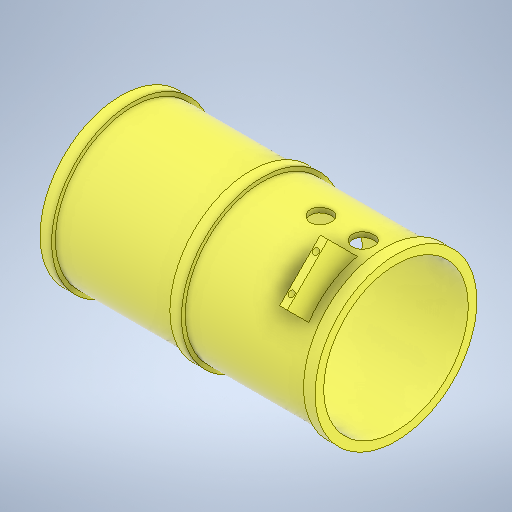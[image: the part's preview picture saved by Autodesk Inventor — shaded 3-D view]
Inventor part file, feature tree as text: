
AUTODESK INVENTOR PART (.ipt)
format: ipt  version: 2025.1 (Build 291241000, 241)  size: 377,856 bytes
history: native  units: mm
features: sketch x8, plane x6, other x4, hole x3, extrude x2, revolve x1
ambient origin geometry x8: Origin, YZ Plane, XZ Plane, XY Plane, X Axis, Y Axis, Z Axis, Center Point
bodies: Body1 (feature_tree)
feature tree (24):
  revolve  "Revolution1"  [1 undecoded]
  hole  "Hole1"  [1 undecoded]
  plane  "Work Plane2"
  hole  "Hole3"  [1 undecoded]
  plane  "Work Plane1"
  hole  "Hole2"  [1 undecoded]
  plane  "Work Plane4"
  plane  "Work Plane5"
  sketch  "Sketch7"  dims[d13=75.0mm d14=6.0mm d15=4.0mm d16=2.0mm d17=90.0deg d18=3.5mm d19=0.0mm d20=40.0mm]
  plane  "Work Plane7"
  sketch  "Sketch8"  dims[d21=22.0mm d22=17.0mm]
  other  "Work Axis2"
  other  "Work Point1"
  other  "Work Point2"
  other  "Work Axis3"
  plane  "Work Plane12"
  extrude  "Extrusion3"  Depth=40.0mm
  extrude  "Extrusion4"  Depth=17.0mm
  sketch  "Sketch2"  dims[d4=84.0mm d6=80.0mm]
  sketch  "Sketch3"  dims[d7=6.0mm d8=6.0mm]
  sketch  "Sketch4"  dims[d9=6.0mm d10=61.5mm]
  sketch  "Sketch5"  dims[d11=63.5mm d12=90.0deg]
  sketch  "Sketch10"  dims[d23=11.0mm d24=6.0mm d25=4.0mm d26=2.0mm d27=90.0deg d28=3.5mm d29=0.0mm]
  sketch  "Sketch11"  dims[d30=40.0mm d31=45.0mm d32=62.0mm d33=14.0mm d34=6.0mm d35=4.0mm d36=2.0mm d37=90.0deg d38=4.0mm d39=0.0mm d41=55.0mm d47=5.969mm d48=45.0deg d49=35.969mm d50=45.0deg d53=110.0mm d54=110.0mm d55=4.0mm d56=30.0mm d57=10.0mm d58=0.0mm d59=32.0mm d60=18.0mm d61=9.0mm d62=3.0mm d63=3.0mm d64=10.0mm d65=0.0mm]
note: 4 required parameter values undecoded (feature->parameter linkage not recoverable at this tier; creation-order binding heuristic only, values carry confidence <= 0.55)